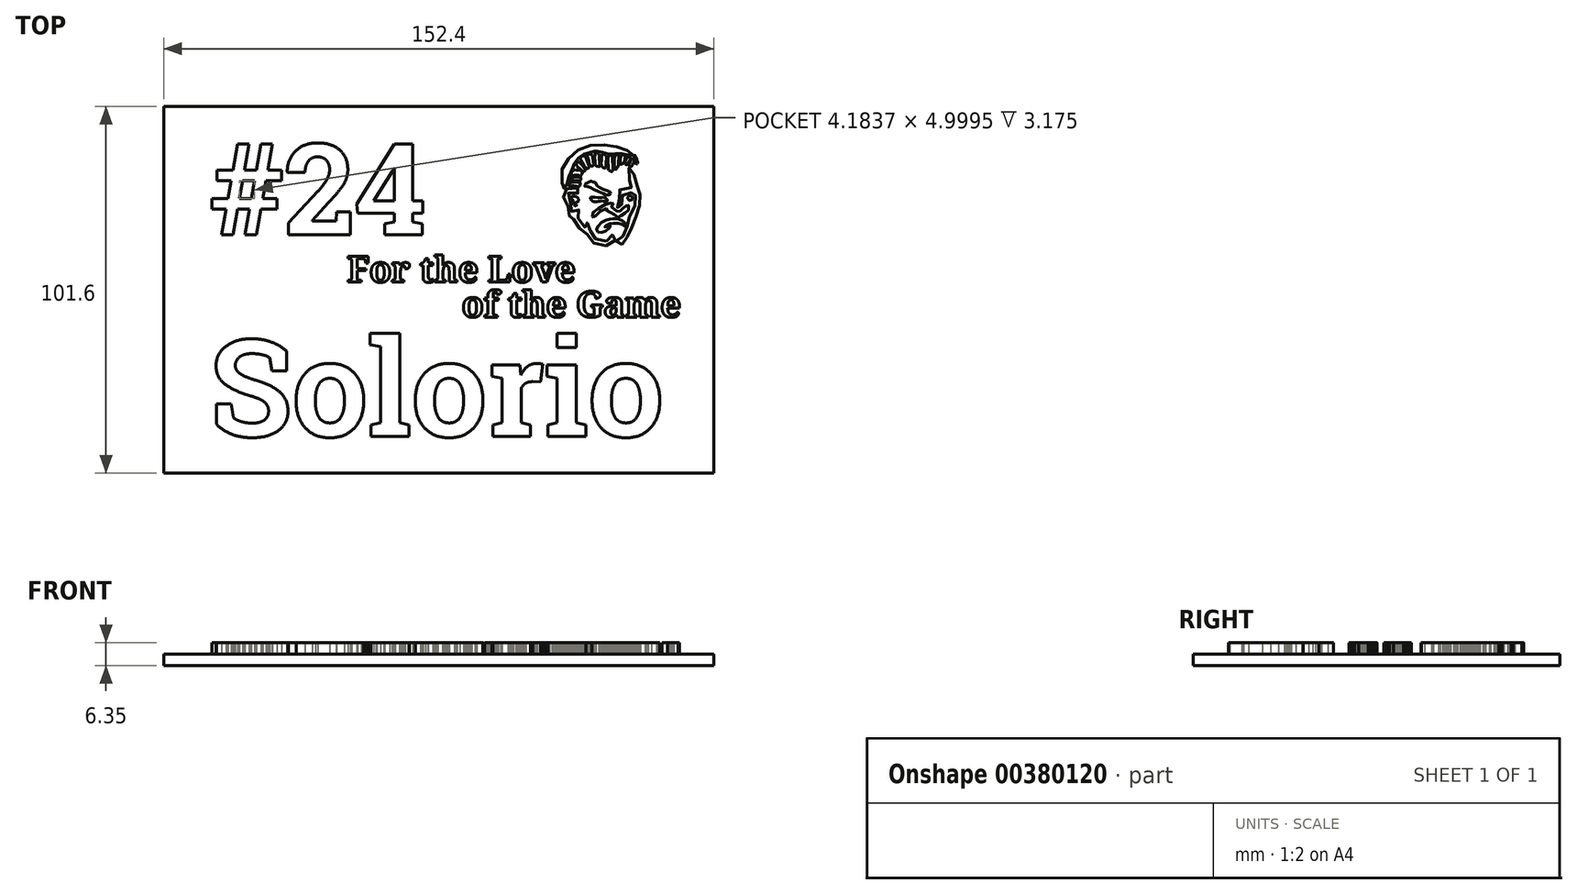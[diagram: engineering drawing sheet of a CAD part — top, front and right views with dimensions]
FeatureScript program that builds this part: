
annotation { "Feature Type Name" : "Feature", "Feature Type Description" : "" }
export const myFeature = defineFeature(function(context is Context, id is Id, definition is map)
    precondition{}
    {
        {
            var Q0;
            Q0=qCreatedBy(makeId("Top.planeOp"),FACE);
            var sketch = newSketch(context, id + "F0", { "sketchPlane" : qUnion([Q0])});
            skLineSegment(sketch, "E0.bottom", {"start": v(-75.13, 26) * mm, "end": v(77.27, 26) * mm});
            skLineSegment(sketch, "E0.top", {"start": v(-75.13, -75.6) * mm, "end": v(77.27, -75.6) * mm});
            skLineSegment(sketch, "E0.left", {"start": v(-75.13, 26) * mm, "end": v(-75.13, -75.6) * mm});
            skLineSegment(sketch, "E0.right", {"start": v(77.27, 26) * mm, "end": v(77.27, -75.6) * mm});
            skSolve(sketch);
        }
        {
            var Q0;
            Q0=makeQuery(id+"F0.imprint","IMPRINT",FACE,{"disambiguationData":[TD([[makeQuery(id+"F0.imprint","IMPRINT",EDGE,{"derivedFrom":sQuery(id+"F0.wireOp",EDGE,"E0.bottom")}),-1.0]])]});
            var sketch = newSketch(context, id + "F1", { "sketchPlane" : qUnion([Q0])});
            skFitSpline(sketch, "E1", {"points": [v(47.57, -11.3) * mm, v(48.35, -11.04) * mm, v(48.7, -10.35) * mm, v(49.04, -9.7) * mm, v(49.57, -9.46) * mm, v(50.02, -9.78) * mm, v(50.06, -10.58) * mm, v(49.74, -11.5) * mm, v(49.1, -12.15) * mm, v(47.63, -12.55) * mm, v(46.12, -12.5) * mm, v(44.61, -12.12) * mm, v(43.38, -11.34) * mm, v(42.6, -10.32) * mm, v(42.24, -9.52) * mm, v(42.15, -9.31) * mm, v(41.34, -8.82) * mm, v(40.33, -8.02) * mm, v(39.44, -7.2) * mm, v(38.67, -6.1) * mm, v(38.42, -5) * mm, v(38.42, -4.22) * mm, v(38.35, -4.2) * mm, v(37.68, -4.39) * mm, v(37.16, -4.27) * mm, v(36.95, -3.72) * mm, v(36.86, -2.5) * mm, v(36.8, -1.48) * mm, v(36.67, -1.07) * mm, v(35.77, 0.2) * mm, v(35.58, 1.07) * mm, v(35.86, 2.13) * mm, v(36.18, 2.7) * mm, v(36.53, 3.12) * mm, v(37.23, 3.22) * mm, v(39.03, 3.4) * mm, v(39.82, 3.34) * mm, v(40.19, 3.09) * mm, v(40.23, 2.45) * mm, v(39.66, 1.98) * mm, v(38.93, 1.9) * mm, v(38.59, 2.03) * mm, v(37.24, 2.03) * mm, v(36.72, 1.65) * mm, v(36.72, 0.85) * mm, v(37.32, -0.2) * mm, v(37.77, -1.18) * mm, v(37.85, -2.09) * mm, v(37.9, -3.1) * mm, v(37.99, -3.1) * mm, v(38.63, -3.1) * mm, v(39.4, -2.76) * mm, v(39.72, -2.59) * mm, v(39.8, -2.7) * mm, v(39.73, -3.22) * mm, v(39.6, -4) * mm, v(39.6, -4.77) * mm, v(40.1, -5.82) * mm, v(41.16, -7.15) * mm, v(41.6, -7.53) * mm, v(41.9, -7.56) * mm, v(41.89, -7.44) * mm, v(41.82, -6.61) * mm, v(42, -6.23) * mm, v(42.5, -6.3) * mm, v(42.8, -6.61) * mm, v(43.05, -7.98) * mm, v(43.22, -8.82) * mm, v(43.51, -9.54) * mm, v(44.12, -10.4) * mm, v(45.11, -11.01) * mm, v(46.32, -11.33) * mm, v(47.57, -11.3) * mm]});
            skFitSpline(sketch, "E2", {"points": [v(47.8, -7.3) * mm, v(47.13, -7.42) * mm, v(47.01, -7.42) * mm, v(47.13, -7.18) * mm, v(48.11, -6.65) * mm, v(49.11, -6.46) * mm, v(50.54, -6.45) * mm, v(51.76, -6.67) * mm, v(52.61, -7.21) * mm, v(52.82, -7.33) * mm, v(52.97, -7.12) * mm, v(52.7, -6.5) * mm, v(52.11, -5.74) * mm, v(50.6, -5.18) * mm, v(49.08, -5.16) * mm, v(48.46, -5.24) * mm, v(47.16, -5.6) * mm, v(45.65, -6.61) * mm, v(44.86, -7.78) * mm, v(44.9, -8.5) * mm, v(45.47, -8.94) * mm, v(46.7, -8.8) * mm, v(47.75, -8.16) * mm, v(48.56, -7.4) * mm, v(48.6, -7.12) * mm, v(47.8, -7.3) * mm]});
            skFitSpline(sketch, "E3", {"points": [v(51.85, -12.22) * mm, v(51.05, -12.44) * mm, v(50.33, -12.28) * mm, v(50.13, -11.73) * mm, v(50.52, -11.04) * mm, v(51.15, -10.86) * mm, v(51.76, -10.57) * mm, v(52.13, -10) * mm, v(52.3, -9.2) * mm, v(52.67, -8.25) * mm, v(53.2, -7.5) * mm, v(53.55, -6.76) * mm, v(53.63, -5.82) * mm, v(53.78, -4.85) * mm, v(54.49, -3.73) * mm, v(55.3, -2.73) * mm, v(55.42, -1.6) * mm, v(55.17, -0.4) * mm, v(55.2, 0.11) * mm, v(55.52, 1.32) * mm, v(55.57, 2.16) * mm, v(55.47, 2.42) * mm, v(54.99, 2.38) * mm, v(54.56, 2.14) * mm, v(53.7, 2.1) * mm, v(52.55, 2.06) * mm, v(52.07, 1.77) * mm, v(51.98, 1.02) * mm, v(52.2, 0.28) * mm, v(52.08, -0.6) * mm, v(51.72, -1.24) * mm, v(51.47, -1.75) * mm, v(51.5, -2.22) * mm, v(51.32, -2.4) * mm, v(50.6, -2.13) * mm, v(50.38, -1.6) * mm, v(50.64, -0.97) * mm, v(51, -0.17) * mm, v(51.06, 0.44) * mm, v(50.78, 1.07) * mm, v(50.66, 1.97) * mm, v(51.18, 2.9) * mm, v(52.12, 3.24) * mm, v(53.3, 3.36) * mm, v(54.52, 3.48) * mm, v(54.66, 3.6) * mm, v(54.38, 3.97) * mm, v(54, 4.8) * mm, v(53.79, 6.28) * mm, v(53.9, 7.94) * mm, v(53.79, 8.9) * mm, v(53.79, 9.1) * mm, v(54.03, 9.04) * mm, v(54.76, 8.52) * mm, v(55.13, 7.38) * mm, v(55.34, 5.97) * mm, v(55.56, 4.72) * mm, v(56.14, 3.87) * mm, v(56.71, 3.56) * mm, v(57.08, 2.91) * mm, v(56.95, 1.93) * mm, v(56.51, 0.55) * mm, v(56.4, -0.31) * mm, v(56.62, -1.36) * mm, v(56.69, -2.19) * mm, v(56.32, -3.56) * mm, v(55.4, -4.86) * mm, v(54.62, -5.8) * mm, v(54.5, -7.08) * mm, v(54.37, -8.24) * mm, v(53.76, -9.26) * mm, v(53.43, -9.82) * mm, v(53.28, -10.59) * mm, v(53.14, -11.27) * mm, v(52.34, -11.95) * mm, v(51.85, -12.22) * mm]});
            skFitSpline(sketch, "E4", {"points": [v(51.65, -4.28) * mm, v(52.13, -3.81) * mm, v(53.02, -3.37) * mm, v(53.66, -2.72) * mm, v(53.77, -1.9) * mm, v(53.38, -1.13) * mm, v(53.21, -1.15) * mm, v(53, -1.68) * mm, v(52.43, -2.14) * mm, v(51.8, -2.46) * mm, v(51.42, -2.92) * mm, v(50.93, -3.27) * mm, v(50.6, -3.17) * mm, v(50.13, -2.68) * mm, v(49.7, -2.46) * mm, v(49.28, -2.45) * mm, v(49, -1.98) * mm, v(49.06, -1.41) * mm, v(49.39, -0.94) * mm, v(49.4, -0.71) * mm, v(48.82, -0.74) * mm, v(47.56, -0.99) * mm, v(45.6, -2.02) * mm, v(44.06, -3.24) * mm, v(43.57, -3.77) * mm, v(43.7, -4.86) * mm, v(43.9, -4.88) * mm, v(44.45, -4.27) * mm, v(46.1, -2.93) * mm, v(47.41, -2.3) * mm, v(47.63, -2.3) * mm, v(47.73, -2.85) * mm, v(48.15, -3.33) * mm, v(48.9, -3.44) * mm, v(49.24, -3.55) * mm, v(49.84, -4.18) * mm, v(50.54, -4.68) * mm, v(51.18, -4.66) * mm, v(51.65, -4.28) * mm]});
            skFitSpline(sketch, "E5", {"points": [v(54.73, 0.39) * mm, v(54.77, 0.82) * mm, v(54.18, 1.2) * mm, v(53.55, 1.02) * mm, v(53.47, 0.3) * mm, v(54.02, 0) * mm, v(54.73, 0.39) * mm]});
            skFitSpline(sketch, "E6", {"points": [v(44.44, -0.47) * mm, v(43.66, -0.25) * mm, v(43.08, 0.44) * mm, v(43.14, 0.75) * mm, v(43.78, 0.8) * mm, v(46.74, 0.78) * mm, v(47.17, 0.7) * mm, v(47.78, -0.13) * mm, v(47.64, -0.32) * mm, v(46.64, -0.26) * mm, v(45.29, -0.32) * mm, v(44.44, -0.47) * mm]});
            skFitSpline(sketch, "E7", {"points": [v(46.65, 1.86) * mm, v(47.46, 1.48) * mm, v(48.33, 1.53) * mm, v(48.69, 2.02) * mm, v(48.54, 2.32) * mm, v(47.26, 2.83) * mm, v(45.32, 3.72) * mm, v(44.79, 4.23) * mm, v(44.53, 4.83) * mm, v(44.13, 5) * mm, v(43.88, 5) * mm, v(43.34, 5.26) * mm, v(43.09, 5.3) * mm, v(42.9, 5.05) * mm, v(42.6, 5.07) * mm, v(42.3, 4.85) * mm, v(42.2, 4.73) * mm, v(41.9, 4.72) * mm, v(41.8, 4.5) * mm, v(41.38, 4.05) * mm, v(41.56, 3.84) * mm, v(42.59, 3.74) * mm, v(43.78, 3.19) * mm, v(46.65, 1.86) * mm]});
            skFitSpline(sketch, "E8", {"points": [v(39.09, -1.2) * mm, v(38.85, -1.02) * mm, v(39.04, -0.63) * mm, v(39.6, -0.4) * mm, v(39.72, 0.33) * mm, v(39.01, 1.06) * mm, v(38.23, 1.1) * mm, v(37.7, 0.65) * mm, v(37.83, 0.29) * mm, v(38.12, 0.15) * mm, v(38.31, -0.34) * mm, v(38.52, -1.23) * mm, v(38.92, -1.63) * mm, v(39.18, -1.51) * mm, v(39.26, -1.2) * mm, v(39.09, -1.2) * mm]});
            skFitSpline(sketch, "E9", {"points": [v(35.18, 4.73) * mm, v(35.4, 3.4) * mm, v(35.76, 3.05) * mm, v(35.87, 3.13) * mm, v(36.08, 3.42) * mm, v(36.43, 3.67) * mm, v(36.66, 4.42) * mm, v(36.6, 5.36) * mm, v(37.02, 6.1) * mm, v(37.15, 6.7) * mm, v(37.23, 7.46) * mm, v(37.88, 8.4) * mm, v(38.45, 9.02) * mm, v(38.56, 9.75) * mm, v(38.74, 10.4) * mm, v(39.17, 10.98) * mm, v(39.64, 11.29) * mm, v(39.78, 11.9) * mm, v(40.12, 12.28) * mm, v(40.85, 12.68) * mm, v(41.65, 12.77) * mm, v(42.03, 12.99) * mm, v(42.91, 13.25) * mm, v(43.49, 13.17) * mm, v(43.91, 13.25) * mm, v(44.22, 13.54) * mm, v(44.87, 13.6) * mm, v(45.62, 13.32) * mm, v(46.3, 13.31) * mm, v(46.91, 13.3) * mm, v(47.51, 12.81) * mm, v(48.11, 12.71) * mm, v(48.8, 12.83) * mm, v(49.39, 12.68) * mm, v(50.13, 12.89) * mm, v(50.83, 12.96) * mm, v(51.35, 12.83) * mm, v(51.87, 12.94) * mm, v(52.53, 12.95) * mm, v(53.18, 12.6) * mm, v(53.93, 12.6) * mm, v(54.48, 12.4) * mm, v(54.65, 12.18) * mm, v(55.03, 12.55) * mm, v(54.73, 12.89) * mm, v(53.9, 13.45) * mm, v(51.53, 14.51) * mm, v(50.44, 14.76) * mm, v(49.1, 15.08) * mm, v(45.83, 15.4) * mm, v(43.17, 15.22) * mm, v(40.97, 14.54) * mm, v(38.6, 13.18) * mm, v(36.98, 11.4) * mm, v(35.34, 9.1) * mm, v(35.2, 8.1) * mm, v(35.18, 4.73) * mm]});
            skFitSpline(sketch, "E10", {"points": [v(39.4, 5) * mm, v(39.96, 4.99) * mm, v(40.23, 4.82) * mm, v(40.1, 4) * mm, v(39.64, 3.78) * mm, v(38.94, 3.9) * mm, v(37.89, 3.94) * mm, v(37.45, 3.8) * mm, v(37.1, 4.04) * mm, v(37.54, 4.84) * mm, v(38.3, 5) * mm, v(39.4, 5) * mm]});
            skFitSpline(sketch, "E11", {"points": [v(37.48, 5.07) * mm, v(37.11, 4.96) * mm, v(36.94, 5.2) * mm, v(37.34, 5.9) * mm, v(37.75, 6.14) * mm, v(39.96, 6.47) * mm, v(40.35, 6.2) * mm, v(40.47, 5.65) * mm, v(40.11, 5.36) * mm, v(39.64, 5.4) * mm, v(38.37, 5.41) * mm, v(37.48, 5.07) * mm]});
            skFitSpline(sketch, "E12", {"points": [v(38.14, 6.82) * mm, v(39.68, 6.88) * mm, v(40, 6.74) * mm, v(40.54, 7) * mm, v(40.85, 7.85) * mm, v(40.67, 8.1) * mm, v(39.1, 8.4) * mm, v(38.41, 8.3) * mm, v(37.9, 7.73) * mm, v(37.48, 6.86) * mm, v(37.68, 6.74) * mm, v(38.14, 6.82) * mm]});
            skFitSpline(sketch, "E13", {"points": [v(39.26, 9.59) * mm, v(41, 8.1) * mm, v(41.32, 7.94) * mm, v(41.68, 8.33) * mm, v(41.53, 8.74) * mm, v(40.44, 10.1) * mm, v(39.87, 10.6) * mm, v(39.5, 10.56) * mm, v(39.13, 10.09) * mm, v(39.26, 9.59) * mm]});
            skFitSpline(sketch, "E14", {"points": [v(40.75, 10.65) * mm, v(40.33, 11.47) * mm, v(40.46, 11.98) * mm, v(41.21, 12.34) * mm, v(41.77, 12.07) * mm, v(42.13, 11.12) * mm, v(42.72, 9.33) * mm, v(42.65, 8.96) * mm, v(42.12, 8.81) * mm, v(41.62, 9.07) * mm, v(40.75, 10.65) * mm]});
            skFitSpline(sketch, "E15", {"points": [v(42.43, 11.4) * mm, v(42.21, 12.24) * mm, v(42.3, 12.64) * mm, v(43, 12.81) * mm, v(43.54, 12.53) * mm, v(43.83, 11.13) * mm, v(44, 9.88) * mm, v(43.65, 9.47) * mm, v(42.94, 9.8) * mm, v(42.43, 11.4) * mm]});
            skFitSpline(sketch, "E16", {"points": [v(44.29, 12.06) * mm, v(44.36, 12.96) * mm, v(44.5, 13.26) * mm, v(44.93, 13.17) * mm, v(45.54, 12.55) * mm, v(45.55, 11.97) * mm, v(45.6, 9.45) * mm, v(45.5, 9.32) * mm, v(44.61, 9.6) * mm, v(44.4, 10.08) * mm, v(44.29, 12.06) * mm]});
            skFitSpline(sketch, "E17", {"points": [v(46.05, 10.51) * mm, v(46.15, 9.53) * mm, v(46.62, 9.04) * mm, v(47.1, 8.88) * mm, v(47.3, 9.08) * mm, v(47.48, 10.9) * mm, v(47.53, 12.07) * mm, v(47.34, 12.46) * mm, v(46.68, 12.84) * mm, v(46.32, 12.79) * mm, v(46.17, 11.97) * mm, v(46.05, 10.51) * mm]});
            skFitSpline(sketch, "E18", {"points": [v(48.03, 8.99) * mm, v(48.11, 8.48) * mm, v(48.48, 8.11) * mm, v(48.94, 7.92) * mm, v(49.21, 8.2) * mm, v(49.24, 10.23) * mm, v(49.16, 12.1) * mm, v(48.83, 12.47) * mm, v(48.44, 12.47) * mm, v(47.98, 12) * mm, v(47.93, 10.87) * mm, v(48.03, 8.99) * mm]});
            skFitSpline(sketch, "E19", {"points": [v(49.71, 9.45) * mm, v(49.86, 8.66) * mm, v(50.13, 8.48) * mm, v(50.3, 8.75) * mm, v(50.76, 9.43) * mm, v(50.85, 10.13) * mm, v(50.93, 12.16) * mm, v(50.81, 12.6) * mm, v(50.31, 12.66) * mm, v(49.83, 12.22) * mm, v(49.7, 11.19) * mm, v(49.71, 9.45) * mm]});
            skFitSpline(sketch, "E20", {"points": [v(51.32, 10.54) * mm, v(51.4, 11.84) * mm, v(51.7, 12.52) * mm, v(52.3, 12.55) * mm, v(52.72, 12.21) * mm, v(52.63, 11.54) * mm, v(52.29, 10.26) * mm, v(51.93, 10.06) * mm, v(51.44, 9.99) * mm, v(51.32, 10.54) * mm]});
            skFitSpline(sketch, "E21", {"points": [v(52.63, 10.38) * mm, v(52.83, 11.01) * mm, v(53.35, 11.9) * mm, v(53.66, 12.08) * mm, v(54.13, 11.71) * mm, v(53.9, 10.95) * mm, v(53.35, 10.1) * mm, v(53.17, 9.86) * mm, v(52.8, 9.99) * mm, v(52.63, 10.38) * mm]});
            skFitSpline(sketch, "E22", {"points": [v(53.86, 10.18) * mm, v(53.7, 9.9) * mm, v(53.81, 9.57) * mm, v(54.15, 9.28) * mm, v(54.42, 9.39) * mm, v(55.14, 10.6) * mm, v(55.26, 11.14) * mm, v(55.02, 11.54) * mm, v(54.8, 11.61) * mm, v(54.48, 11.27) * mm, v(53.86, 10.18) * mm]});
            skFitSpline(sketch, "E23", {"points": [v(55.24, 11.7) * mm, v(55.54, 11.38) * mm, v(55.58, 10.83) * mm, v(55.47, 10.49) * mm, v(55.7, 10.04) * mm, v(55.92, 10.02) * mm, v(56.2, 10.63) * mm, v(56.05, 10.85) * mm, v(55.85, 11.61) * mm, v(55.63, 12) * mm, v(55.42, 12.46) * mm, v(55.15, 12.4) * mm, v(55.09, 11.93) * mm, v(55.24, 11.7) * mm]});
            skText(sketch, "E24", { "text": "For the Love", "fontName": "NotoSerif-Bold.ttf"});
            skText(sketch, "E25", { "text": "of the Game", "fontName": "NotoSerif-Bold.ttf"});
            skText(sketch, "E26", { "text": "#24", "fontName": "RobotoSlab-Bold.ttf"});
            skText(sketch, "E27", { "text": "Solorio", "fontName": "RobotoSlab-Bold.ttf"});
            const initialGuessF1  = {"E24": [-0.02433, -0.0227, 1, 0, 0.00716], "E25": [0.00742, -0.0324, 1, 0, 0.00716], "E26": [-0.06243, -0.00956, 1, 0, 0.0254], "E27": [-0.06243, -0.06544, 1, 0, 0.02705]};
            skSetInitialGuess(sketch, initialGuessF1);
            skSolve(sketch);
        }
        {
            var Q0;
            Q0=qSketchRegion(id+"F0",true);
            extrude(context, id + "F2", {"entities" : qUnion([Q0]), "depth" : 3.17 * mm});
        }
        {
            var Q0;
            Q0=qSketchRegion(id+"F1",true);
            extrude(context, id + "F3", {"entities" : qUnion([Q0]), "operationType" : NewBodyOperationType.ADD, "depth" : 6.35 * mm});
        }
    });
